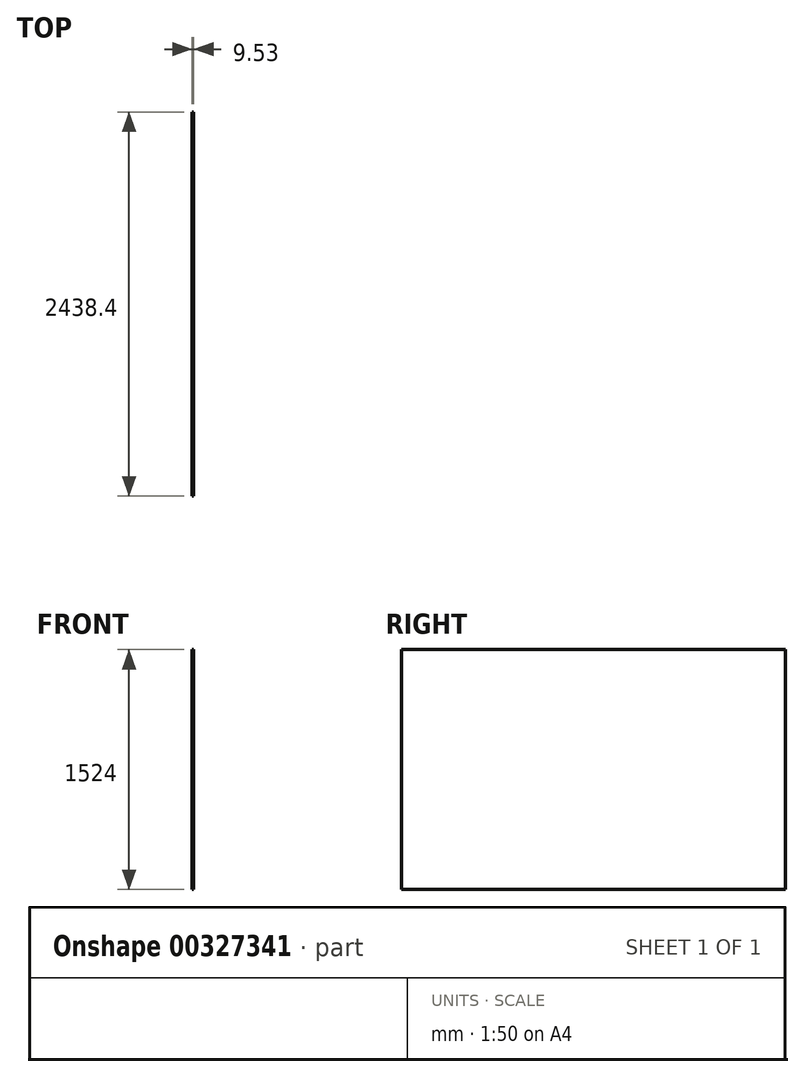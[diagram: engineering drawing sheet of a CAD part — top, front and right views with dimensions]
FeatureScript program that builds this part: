
annotation { "Feature Type Name" : "Feature", "Feature Type Description" : "" }
export const myFeature = defineFeature(function(context is Context, id is Id, definition is map)
    precondition{}
    {
        {
            var Q0;
            Q0=qCreatedBy(makeId("Right.planeOp"),FACE);
            var sketch = newSketch(context, id + "F0", { "sketchPlane" : qUnion([Q0])});
            skLineSegment(sketch, "E0.bottom", {"start": v(-1287.71, 348.94) * mm, "end": v(1150.69, 348.94) * mm});
            skLineSegment(sketch, "E0.top", {"start": v(-1287.71, -1175.06) * mm, "end": v(1150.69, -1175.06) * mm});
            skLineSegment(sketch, "E0.left", {"start": v(-1287.71, 348.94) * mm, "end": v(-1287.71, -1175.06) * mm});
            skLineSegment(sketch, "E0.right", {"start": v(1150.69, 348.94) * mm, "end": v(1150.69, -1175.06) * mm});
            skSolve(sketch);
        }
        {
            var Q0;
            Q0 = qSketchRegion(id + "F0", true);
            extrude(context, id + "F1", {"entities" : qUnion([Q0]), "depth" : 9.52 * mm});
        }
    });
